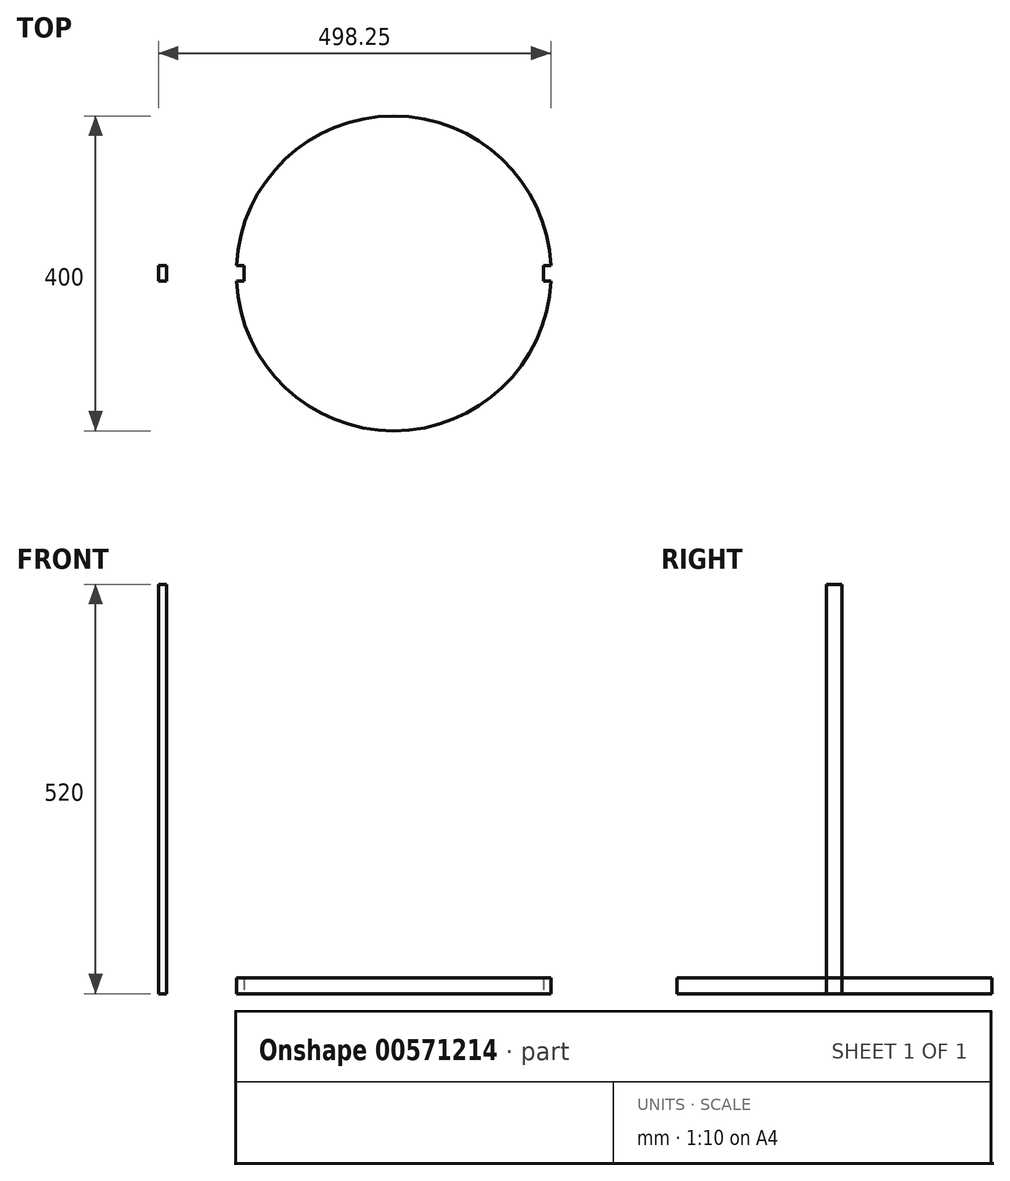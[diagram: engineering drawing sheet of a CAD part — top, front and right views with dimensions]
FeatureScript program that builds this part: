
annotation { "Feature Type Name" : "Feature", "Feature Type Description" : "" }
export const myFeature = defineFeature(function(context is Context, id is Id, definition is map)
    precondition{}
    {
        {
            var Q0;
            Q0=qCreatedBy(makeId("Top.planeOp"),FACE);
            var sketch = newSketch(context, id + "F0", { "sketchPlane" : qUnion([Q0])});
            skLineSegment(sketch, "E0.bottom", {"start": v(-298.5, 10) * mm, "end": v(-288.5, 10) * mm});
            skLineSegment(sketch, "E0.top", {"start": v(-298.5, -10) * mm, "end": v(-288.5, -10) * mm});
            skLineSegment(sketch, "E0.left", {"start": v(-298.5, 10) * mm, "end": v(-298.5, -10) * mm});
            skLineSegment(sketch, "E0.right", {"start": v(-288.5, 10) * mm, "end": v(-288.5, -10) * mm});
            skPoint(sketch, "E0.middle", {"position": v(-293.5, 0) * mm});
            skSolve(sketch);
        }
        {
            var Q0;
            Q0 = qSketchRegion(id + "F0", true);
            extrude(context, id + "F1", {"entities" : qUnion([Q0]), "depth" : 520 * mm, "offsetDistance" : 25.4 * mm});
        }
        {
            var Q0;
            Q0=qCreatedBy(makeId("Top.planeOp"),FACE);
            var sketch = newSketch(context, id + "F2", { "sketchPlane" : qUnion([Q0])});
            skCircle(sketch, "E1", {"center": v(0, 0) * mm, "radius": 200 * mm});
            skSolve(sketch);
        }
        {
            var Q0;
            Q0=makeQuery(id+"F2.imprint","IMPRINT",FACE,{"disambiguationData":[TD([[makeQuery(id+"F2.imprint","IMPRINT",EDGE,{"derivedFrom":sQuery(id+"F2.wireOp",EDGE,"E1")}),1.0]])]});
            extrude(context, id + "F3", {"entities" : qUnion([Q0]), "operationType" : NewBodyOperationType.ADD, "depth" : 20 * mm, "offsetDistance" : 25.4 * mm});
        }
        {
            var Q0;
            Q0=qCreatedBy(makeId("Top.planeOp"),FACE);
            var sketch = newSketch(context, id + "F4", { "sketchPlane" : qUnion([Q0])});
            skLineSegment(sketch, "E2.bottom", {"start": v(-190.03, 10) * mm, "end": v(-200.03, 10) * mm});
            skLineSegment(sketch, "E2.top", {"start": v(-200.03, -10) * mm, "end": v(-190.03, -10) * mm});
            skLineSegment(sketch, "E2.left", {"start": v(-200.03, 10) * mm, "end": v(-200.03, -10) * mm});
            skLineSegment(sketch, "E2.right", {"start": v(-190.03, 10) * mm, "end": v(-190.03, -10) * mm});
            skPoint(sketch, "E2.middle", {"position": v(-195.03, 0) * mm});
            skSolve(sketch);
        }
        {
            var Q0;
            Q0 = qSketchRegion(id + "F4", true);
            extrude(context, id + "F5", {"entities" : qUnion([Q0]), "operationType" : NewBodyOperationType.REMOVE, "depth" : 20 * mm, "offsetDistance" : 25.4 * mm});
        }
        {
            var Q0;
            Q0=qCreatedBy(makeId("Top.planeOp"),FACE);
            var sketch = newSketch(context, id + "F6", { "sketchPlane" : qUnion([Q0])});
            skLineSegment(sketch, "E3.bottom", {"start": v(190.4, 10) * mm, "end": v(200.4, 10) * mm});
            skLineSegment(sketch, "E3.top", {"start": v(190.4, -10) * mm, "end": v(200.4, -10) * mm});
            skLineSegment(sketch, "E3.left", {"start": v(190.4, 10) * mm, "end": v(190.4, -10) * mm});
            skLineSegment(sketch, "E3.right", {"start": v(200.4, 10) * mm, "end": v(200.4, -10) * mm});
            skPoint(sketch, "E3.middle", {"position": v(195.4, 0) * mm});
            skSolve(sketch);
        }
        {
            var Q0;
            Q0 = qSketchRegion(id + "F6", true);
            extrude(context, id + "F7", {"entities" : qUnion([Q0]), "operationType" : NewBodyOperationType.REMOVE, "depth" : 20 * mm, "offsetDistance" : 25.4 * mm});
        }
    });
